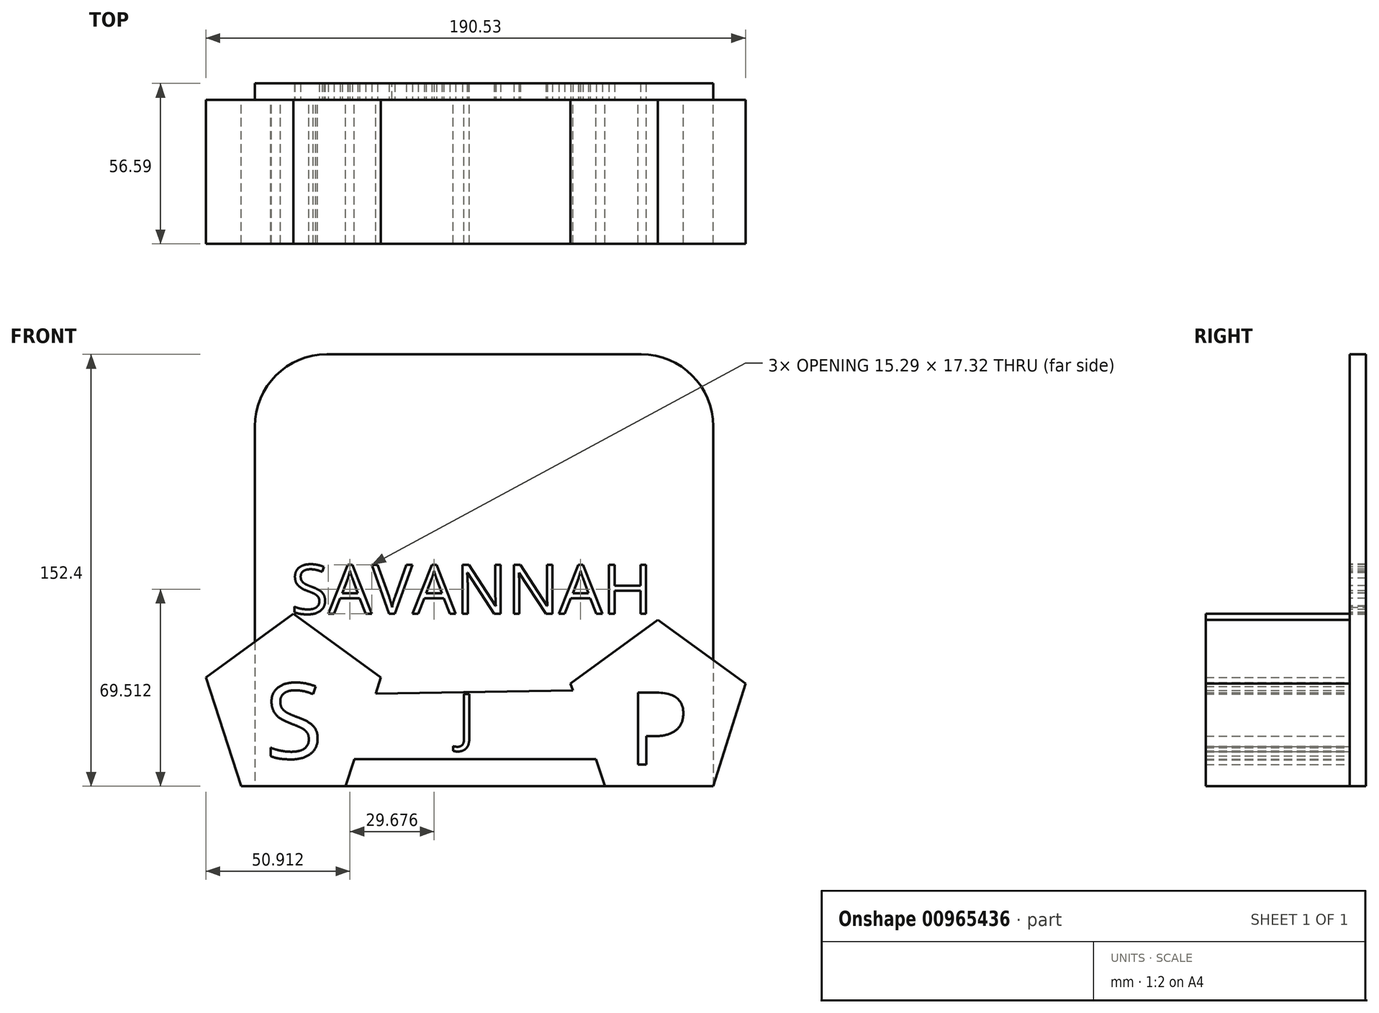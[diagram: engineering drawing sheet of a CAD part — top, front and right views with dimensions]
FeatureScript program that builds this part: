
annotation { "Feature Type Name" : "Feature", "Feature Type Description" : "" }
export const myFeature = defineFeature(function(context is Context, id is Id, definition is map)
    precondition{}
    {
        {
            var Q0;
            Q0=qCreatedBy(makeId("Front.planeOp"),FACE);
            var sketch = newSketch(context, id + "F0", { "sketchPlane" : qUnion([Q0])});
            skLineSegment(sketch, "E0.0", {"start": v(90.2, -25.16) * mm, "end": v(51.98, -25.16) * mm});
            skLineSegment(sketch, "E0.1", {"start": v(51.98, -25.16) * mm, "end": v(48.78, -15.63) * mm});
            skLineSegment(sketch, "E0.2", {"start": v(39.8, 11.07) * mm, "end": v(70.72, 33.53) * mm});
            skLineSegment(sketch, "E0.3", {"start": v(70.72, 33.53) * mm, "end": v(101.63, 11.07) * mm});
            skLineSegment(sketch, "E0.4", {"start": v(101.63, 11.07) * mm, "end": v(90.2, -25.16) * mm});
            skPoint(sketch, "E0.0.midPoint", {"position": v(71.08, -25.16) * mm});
            skLineSegment(sketch, "E1", {"start": v(48.78, -15.63) * mm, "end": v(-36.53, -15.63) * mm});
            skLineSegment(sketch, "E2", {"start": v(-36.53, -15.63) * mm, "end": v(-36.53, -15.9) * mm});
            skLineSegment(sketch, "E3.0", {"start": v(-39.54, -25.16) * mm, "end": v(-76.43, -25.16) * mm});
            skLineSegment(sketch, "E3.1", {"start": v(-76.43, -25.16) * mm, "end": v(-88.9, 13.23) * mm});
            skLineSegment(sketch, "E3.2", {"start": v(-88.9, 13.23) * mm, "end": v(-57.98, 35.69) * mm});
            skLineSegment(sketch, "E3.3", {"start": v(-57.98, 35.69) * mm, "end": v(-27.07, 13.23) * mm});
            skLineSegment(sketch, "E3.4", {"start": v(-27.07, 13.23) * mm, "end": v(-28.91, 7.55) * mm});
            skPoint(sketch, "E3.0.midPoint", {"position": v(-57.98, -25.16) * mm});
            skPoint(sketch, "E4.orphan", {"position": v(-36.53, 7.55) * mm});
            skPoint(sketch, "E0.cCircle.center.orphan", {"position": v(71.08, 0) * mm});
            skText(sketch, "E5", { "text": "S", "fontName": "OpenSans-Regular.ttf"});
            skText(sketch, "E6", { "text": "J\n", "fontName": "OpenSans-Regular.ttf"});
            skText(sketch, "E7", { "text": "P", "fontName": "OpenSans-Regular.ttf"});
            skLineSegment(sketch, "E8.trimOffspring", {"start": v(40.64, 8.58) * mm, "end": v(39.8, 11.07) * mm});
            skLineSegment(sketch, "E9.trimOffspring", {"start": v(-36.53, -15.9) * mm, "end": v(-39.54, -25.16) * mm});
            skPoint(sketch, "E3.cCircle.center.orphan", {"position": v(-57.98, 3.18) * mm});
            skLineSegment(sketch, "E10", {"start": v(-28.91, 7.55) * mm, "end": v(40.64, 8.58) * mm});
            const initialGuessF0  = {"E5": [-0.06796, -0.01535, 1, 0, 0.02665], "E6": [0.00013, -0.00869, 1, 0, 0.01624], "E7": [0.06014, -0.01746, 1, 0, 0.02552]};
            skSetInitialGuess(sketch, initialGuessF0);
            skSolve(sketch);
        }
        {
            var Q0;
            Q0=makeQuery(id+"F0.imprint","IMPRINT",FACE,{"disambiguationData":[TD([[makeQuery(id+"F0.imprint","IMPRINT",EDGE,{"derivedFrom":sQuery(id+"F0.wireOp",EDGE,"E0.0")}),-1.0]])]});
            extrude(context, id + "F1", {"entities" : qUnion([Q0]), "depth" : 50.8 * mm, "offsetDistance" : 25.4 * mm});
        }
        {
            var Q0;
            Q0=makeQuery(id+"F1.opExtrude","SWEPT_FACE",FACE,{"disambiguationData":[OSD([sQuery(id+"F0.wireOp",EDGE,"E0.0")])]});
            var sketch = newSketch(context, id + "F2", { "sketchPlane" : qUnion([Q0])});
            skLineSegment(sketch, "E11.bottom", {"start": v(90.2, 0) * mm, "end": v(-71.6, 0) * mm});
            skLineSegment(sketch, "E11.top", {"start": v(90.2, -5.8) * mm, "end": v(-71.6, -5.8) * mm});
            skLineSegment(sketch, "E11.left", {"start": v(90.2, 0) * mm, "end": v(90.2, -5.8) * mm});
            skLineSegment(sketch, "E11.right", {"start": v(-71.6, 0) * mm, "end": v(-71.6, -5.8) * mm});
            skSolve(sketch);
        }
        {
            var Q0;
            Q0=makeQuery(id+"F2.imprint","IMPRINT",FACE,{"disambiguationData":[TD([[makeQuery(id+"F2.imprint","IMPRINT",EDGE,{"derivedFrom":sQuery(id+"F2.wireOp",EDGE,"E11.top")}),-1.0]])]});
            extrude(context, id + "F3", {"entities" : qUnion([Q0]), "operationType" : NewBodyOperationType.ADD, "oppositeDirection" : true, "depth" : 152.4 * mm, "offsetDistance" : 25.4 * mm});
        }
        {
            var Q0;
            {var subQ2=sQuery(id+"F2.wireOp",EDGE,"E11.bottom");var subQ9=sQuery(id+"F0.wireOp",EDGE,"E0.2");Q0=makeQuery(id+"F3.boolean.opBoolean","SPLIT",FACE,{"disambiguationData":[TD([makeQuery(id+"F1.opExtrude","SWEPT_FACE",FACE,{"disambiguationData":[OSD([subQ9])]})])],"derivedFrom":makeQuery(id+"F3.opExtrude","SWEPT_FACE",FACE,{"disambiguationData":[OSD([subQ2])]})});}
            var sketch = newSketch(context, id + "F4", { "sketchPlane" : qUnion([Q0])});
            skText(sketch, "E12", { "text": "SAVANNAH", "fontName": "OpenSans-Regular.ttf"});
            const initialGuessF4  = {"E12": [-0.0589, 0.03569, 1, 0, 0.0174]};
            skSetInitialGuess(sketch, initialGuessF4);
            skSolve(sketch);
        }
        {
            var Q0;
            Q0 = qSketchRegion(id + "F4", true);
            extrude(context, id + "F5", {"entities" : qUnion([Q0]), "operationType" : NewBodyOperationType.REMOVE, "endBound" : BoundingType.THROUGH_ALL, "oppositeDirection" : true, "depth" : 25.4 * mm, "offsetDistance" : 25.4 * mm});
        }
        {
            var Q0;
            Q0=makeQuery(id+"F3.opExtrude","CAP_EDGE",EDGE,{"disambiguationData":[OSD([sQuery(id+"F2.wireOp",EDGE,"E11.left")])],"isStart":false});
            var Q1;
            Q1=makeQuery(id+"F3.opExtrude","CAP_EDGE",EDGE,{"disambiguationData":[OSD([sQuery(id+"F2.wireOp",EDGE,"E11.right")])],"isStart":false});
            fillet(context, id + "F6", {"entities" : qUnion([Q0, Q1]), "radius" : 25.4 * mm, "tangentPropagation" : true, "allowEdgeOverflow" : false});
        }
    });
